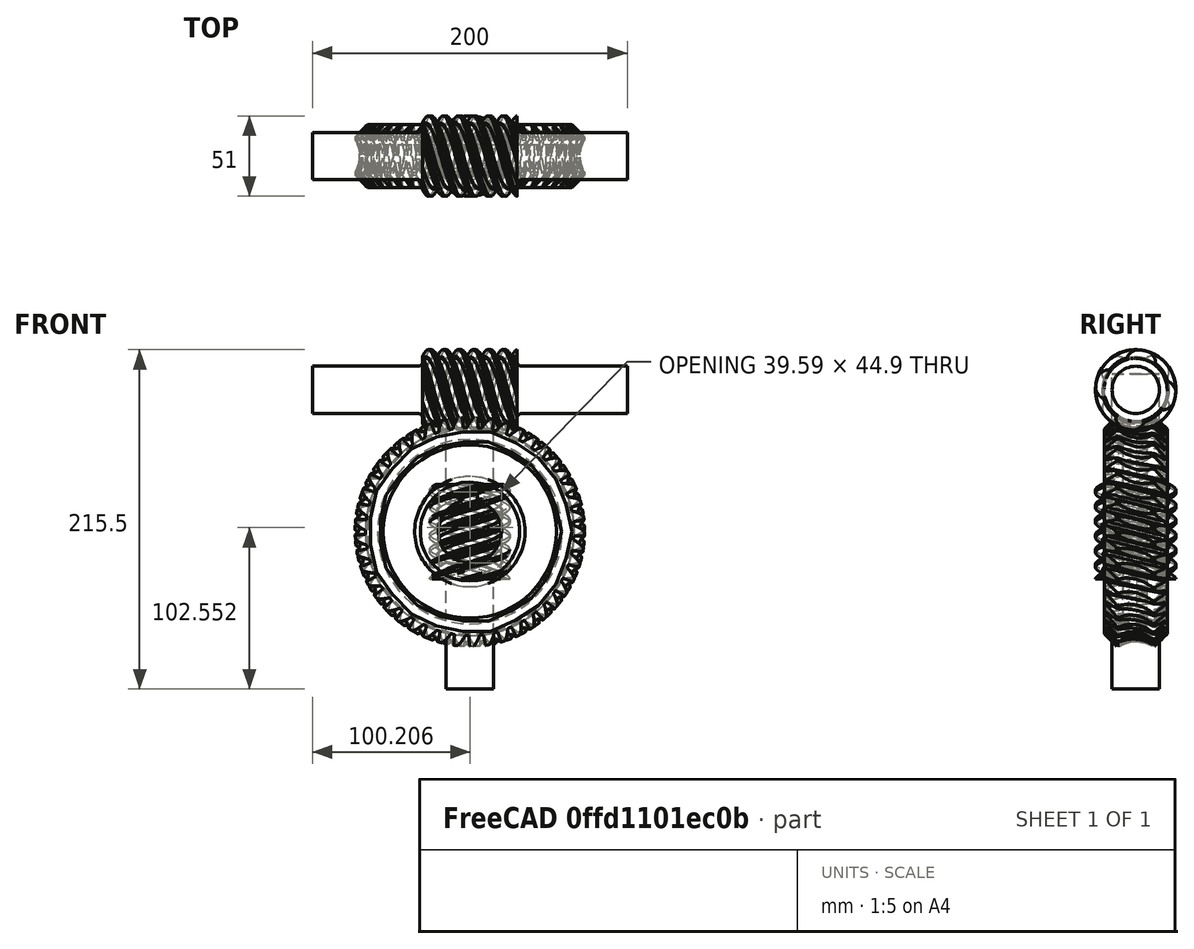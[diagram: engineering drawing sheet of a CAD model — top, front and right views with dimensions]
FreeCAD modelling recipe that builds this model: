
FCSTD DOCUMENT  (FreeCAD 0.18R16146 (Git))
Label: 132 - ENGRENAGEM SEM FIM
License: All rights reserved
LicenseURL: http://en.wikipedia.org/wiki/All_rights_reserved
objects: Part::Feature×13, Part::Cut×10, Part::Cylinder×6, Part::MultiFuse×4, Part::Cone×3, Part::FeaturePython×2, Part::Torus×1, Part::Box×1, Part::Helix×1, Part::Sweep×1, Part::Fillet×1
note: 43 computed .brp shape members not serialized (recipe doc carries the construction recipe); baked Part::Feature solids carry a one-line shape summary decoded from their .brp

FEATURE [Part::FeaturePython] InvoluteGear  # WARN: FeaturePython — macro-defined, semantics opaque (R4)
  Placement = pos=(0,0,-20) rot=(0,0,1;0rad)
  backlash = 0
  beta = 14.93
  clearance = 0.25
  double_helix = false
  head = 0
  height = 40
  module = 3
  numpoints = 6
  pressure_angle = 20
  reversed_backlash = false
  shift = 0
  simple = false
  teeth = 45
  undercut = false
FEATURE [Part::Torus] Torus
  Angle1 = -180
  Angle2 = 180
  Angle3 = 360
  AttacherType = Attacher::AttachEngine3D
  Radius1 = 90
  Radius2 = 20
FEATURE [Part::Cut] Cut
  Base = -> InvoluteGear
  Tool = -> Torus
FEATURE [Part::Cone] Cone
  Angle = 360
  AttacherType = Attacher::AttachEngine3D
  Height = 85
  Radius1 = 85
  Radius2 = 0
FEATURE [Part::Cylinder] Cylinder
  Angle = 360
  AttacherType = Attacher::AttachEngine3D
  Height = 30
  Radius = 100
FEATURE [Part::Cut] Cut001
  Base = -> Cylinder
  Tool = -> Cone
FEATURE [Part::Feature] Cut001001  label="Cut002"
  Placement = pos=(0,0,0) rot=(1,0,0;3.14159rad)
  shape: bbox 200 x 200 x 30 mm, 4 faces (baked)
FEATURE [Part::Cut] Cut001002
  Base = -> Cut
  Tool = -> Cut001
FEATURE [Part::Cut] Cut001003
  Base = -> Cut001002
  Tool = -> Cut001001
FEATURE [Part::Cone] Cone001
  Angle = 360
  AttacherType = Attacher::AttachEngine3D
  Height = 18
  Radius1 = 60
  Radius2 = 55
FEATURE [Part::Cone] Cone002
  Angle = 360
  AttacherType = Attacher::AttachEngine3D
  Height = 18
  Radius1 = 30
  Radius2 = 35
FEATURE [Part::Cut] Cut001004
  Base = -> Cone001
  Placement = pos=(0,0,-25) rot=(0,0,1;0rad)
  Tool = -> Cone002
FEATURE [Part::Feature] Cut001004001  label="Cut001005"
  Placement = pos=(0,5e-15,26) rot=(1,0,0;3.14159rad)
  shape: bbox 120 x 120 x 18 mm, 4 faces (baked)
FEATURE [Part::Cut] Cut001004002
  Base = -> Cut001003
  Tool = -> Cut001004
FEATURE [Part::Cut] Cut001004003
  Base = -> Cut001004002
  Tool = -> Cut001004001
FEATURE [Part::Cylinder] Cylinder001
  Angle = 360
  AttacherType = Attacher::AttachEngine3D
  Height = 50
  Radius = 20
FEATURE [Part::Box] Box  label="Cube"
  AttacherType = Attacher::AttachEngine3D
  Height = 50
  Length = 10
  Placement = pos=(-5,15,0) rot=(0,0,1;0rad)
  Width = 10
FEATURE [Part::MultiFuse] Fusion
  Placement = pos=(0,0,-25) rot=(0,0,1;0rad)
  Shapes = -> [Cylinder001,Box]
FEATURE [Part::Cut] Cut001004004
  Base = -> Cut001004003
  Placement = pos=(0,0,0) rot=(1,0,0;1.5708rad)
  Tool = -> Fusion
FEATURE [Part::Helix] Helix
  Angle = 0
  AttacherType = Attacher::AttachEngine3D
  Height = 100
  LocalCoord = 0
  Pitch = 37.7
  Radius = 22.5
  Style = 1
FEATURE [Part::Feature] Edge
  shape: bbox 1.34 x 0.1588 x 2e-07 mm, 0 faces, 0 solids (baked)
FEATURE [Part::Feature] Edge001
  shape: bbox 1.178 x 0.1465 x 2e-07 mm, 0 faces, 0 solids (baked)
FEATURE [Part::Feature] Edge002
  shape: bbox 3.265 x 1.407 x 2e-07 mm, 0 faces, 0 solids (baked)
FEATURE [Part::Feature] Edge003
  shape: bbox 0.01895 x 1.966 x 2e-07 mm, 0 faces, 0 solids (baked)
FEATURE [Part::Feature] Edge004
  shape: bbox 3.265 x 1.407 x 2e-07 mm, 0 faces, 0 solids (baked)
FEATURE [Part::Feature] Edge005
  shape: bbox 1.178 x 0.1465 x 2e-07 mm, 0 faces, 0 solids (baked)
FEATURE [Part::Feature] Edge006
  shape: bbox 1.34 x 0.1588 x 2e-07 mm, 0 faces, 0 solids (baked)
FEATURE [Part::Feature] Edge007
  shape: bbox 1.242 x 0.9261 x 2e-07 mm, 0 faces, 0 solids (baked)
FEATURE [Part::Feature] Edge149
  shape: bbox 1.242 x 0.9261 x 2e-07 mm, 0 faces, 0 solids (baked)
FEATURE [Part::Feature] Edge150
  shape: bbox 2e-07 x 6.572 x 2e-07 mm, 0 faces, 0 solids (baked)
FEATURE [Part::MultiFuse] Fusion001
  Placement = pos=(0,0,0) rot=(1,0,0;1.83137rad)
  Shapes = -> [Edge150,Edge149,Edge,Edge001,Edge002,Edge003,Edge004,Edge005,Edge006,Edge007]
FEATURE [Part::Sweep] Sweep
  Frenet = true
  Sections = -> [Fusion001]
  Solid = true
  Spine = -> Helix
  Transition = 1
FEATURE [Part::FeaturePython] Array  # Draft array (typed FeaturePython)
  Angle = 360
  ArrayType = 1
  Axis = (0,0,1)
  Base = -> Sweep
  Center = (0,0,0)
  Fuse = false
  IntervalAxis = (0,0,0)
  IntervalX = (1,0,0)
  IntervalY = (0,1,0)
  IntervalZ = (0,0,1)
  NumberPolar = 4
  NumberX = 2
  NumberY = 2
  NumberZ = 1
FEATURE [Part::Cylinder] Cylinder002
  Angle = 360
  AttacherType = Attacher::AttachEngine3D
  Height = 100
  Radius = 20
FEATURE [Part::MultiFuse] Fusion002
  Placement = pos=(0,0,-50) rot=(0,0,1;0rad)
  Shapes = -> [Array,Cylinder002]
FEATURE [Part::Cylinder] Cylinder003
  Angle = 360
  AttacherType = Attacher::AttachEngine3D
  Height = 30
  Placement = pos=(0,0,30) rot=(0,0,1;0rad)
  Radius = 30
FEATURE [Part::Cylinder] Cylinder004
  Angle = 360
  AttacherType = Attacher::AttachEngine3D
  Height = 30
  Placement = pos=(4e-15,0,-30) rot=(0,1,0;3.14159rad)
  Radius = 30
FEATURE [Part::Cut] Cut001004005
  Base = -> Fusion002
  Tool = -> Cylinder003
FEATURE [Part::Cut] Cut001004006
  Base = -> Cut001004005
  Tool = -> Cylinder004
FEATURE [Part::Cylinder] Cylinder005
  Angle = 360
  AttacherType = Attacher::AttachEngine3D
  Height = 200
  Placement = pos=(0,0,-100) rot=(0,0,1;0rad)
  Radius = 15
FEATURE [Part::MultiFuse] Fusion003
  Shapes = -> [Cut001004006,Cylinder005]
FEATURE [Part::Fillet] Fillet
  Base = -> Fusion003
  Edges = 2 edges r=3: [Edge2,Edge231]
FEATURE [Part::Feature] Fillet001
  Placement = pos=(-2e-14,0,90) rot=(0,1,0;4.71239rad)
  shape: bbox 200 x 72.14 x 72.14 mm, 103 faces (baked)
